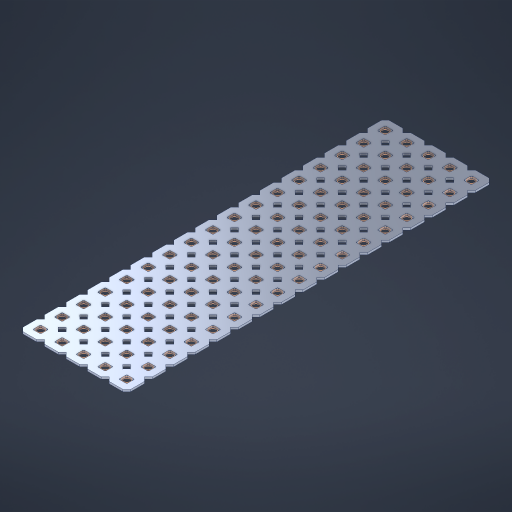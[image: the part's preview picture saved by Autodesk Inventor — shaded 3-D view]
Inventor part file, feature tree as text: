
AUTODESK INVENTOR PART (.ipt)
format: ipt  version: 2023 (Build 270158000, 158)  size: 1,245,696 bytes
history: native  units: in
note: dims shown in document units (in); Inventor stores cm internally (conversion verified against a paired STEP export)
features: other x86, extrude x84, sketch x2, pattern_linear x1
ambient origin geometry x8: Origin, YZ Plane, XZ Plane, XY Plane, X Axis, Y Axis, Z Axis, Center Point
bodies: Solid1 (feature_tree), Body (feature_tree)
feature tree (173):
  pattern_linear  "Rectangular Pattern1"  Spacing1=0.09in  [1 undecoded]
  sketch  "Sketch1"  dims[d1=0.5in]
  sketch  "Sketch2"  dims[d2=0.182in d3=0.09in d4=0.09in d5=0.09in d6=0.09in d7=0.09in d8=0.09in d9=0.09in d10=0.09in d11=0.02in d13=0.0in d14=0.172in d15=0.0625in d16=0.0in d19=0.5in d22=0.5in]
  other  "Srf1"
  other  "Srf126"
  other  "Srf127"
  other  "Srf128"
  other  "Srf129"
  other  "Srf130"
  other  "Srf131"
  other  "Srf250"
  other  "Srf251"
  other  "Srf252"
  other  "Srf253"
  other  "Srf254"
  other  "Srf255"
  other  "Srf256"
  other  "Srf257"
  other  "Srf258"
  other  "Srf259"
  other  "Srf268"
  other  "Srf269"
  other  "Srf270"
  other  "Srf271"
  other  "Srf272"
  other  "Srf273"
  other  "Srf274"
  other  "Srf275"
  other  "Srf276"
  other  "Srf277"
  other  "Srf278"
  other  "Srf279"
  other  "Srf280"
  other  "Srf281"
  other  "Srf282"
  other  "Srf283"
  other  "Srf284"
  other  "Srf293"
  other  "Srf294"
  other  "Srf295"
  other  "Srf296"
  other  "Srf297"
  other  "Srf298"
  other  "Srf299"
  other  "Srf300"
  other  "Srf301"
  other  "Srf302"
  other  "Srf303"
  other  "Srf304"
  other  "Srf305"
  other  "Srf306"
  other  "Srf307"
  other  "Srf308"
  other  "Srf309"
  other  "Srf318"
  other  "Srf319"
  other  "Srf320"
  other  "Srf321"
  other  "Srf322"
  other  "Srf323"
  other  "Srf324"
  other  "Srf325"
  other  "Srf326"
  other  "Srf327"
  other  "Srf328"
  other  "Srf329"
  other  "Srf330"
  other  "Srf331"
  other  "Srf332"
  other  "Srf333"
  other  "Srf334"
  other  "Srf343"
  other  "Srf344"
  other  "Srf345"
  other  "Srf346"
  other  "Srf347"
  other  "Srf348"
  other  "Srf349"
  other  "Srf350"
  other  "Srf351"
  other  "Srf352"
  other  "Srf353"
  other  "Srf354"
  other  "Srf355"
  other  "Srf356"
  other  "Srf357"
  other  "Srf358"
  other  "Srf359"
  other  "Circle"
  extrude  "ExtrusionSrf126"  Depth=0.09in
  extrude  "ExtrusionSrf127"  Depth=0.09in
  extrude  "ExtrusionSrf128"  Depth=0.09in
  extrude  "ExtrusionSrf129"  Depth=0.09in
  extrude  "ExtrusionSrf130"  Depth=0.09in
  extrude  "ExtrusionSrf131"  Depth=0.09in
  extrude  "ExtrusionSrf250"  Depth=0.09in
  extrude  "ExtrusionSrf251"  Depth=0.02in
  extrude  "ExtrusionSrf252"  TaperAngle=0.0deg  [1 undecoded]
  extrude  "ExtrusionSrf253"  Depth=0.5in
  extrude  "ExtrusionSrf254"  Depth=0.5in TaperAngle=0.0deg
  extrude  "ExtrusionSrf255"  Depth=0.5in
  extrude  "ExtrusionSrf256"  Depth=0.5in
  extrude  "ExtrusionSrf257"  [1 undecoded]
  extrude  "ExtrusionSrf258"  [1 undecoded]
  extrude  "ExtrusionSrf259"  [1 undecoded]
  extrude  "ExtrusionSrf268"  [1 undecoded]
  extrude  "ExtrusionSrf269"  [1 undecoded]
  extrude  "ExtrusionSrf270"  [1 undecoded]
  extrude  "ExtrusionSrf271"  [1 undecoded]
  extrude  "ExtrusionSrf272"  [1 undecoded]
  extrude  "ExtrusionSrf273"  [1 undecoded]
  extrude  "ExtrusionSrf274"  [1 undecoded]
  extrude  "ExtrusionSrf275"  [1 undecoded]
  extrude  "ExtrusionSrf276"  [1 undecoded]
  extrude  "ExtrusionSrf277"  [1 undecoded]
  extrude  "ExtrusionSrf278"  [1 undecoded]
  extrude  "ExtrusionSrf279"  [1 undecoded]
  extrude  "ExtrusionSrf280"  [1 undecoded]
  extrude  "ExtrusionSrf281"  [1 undecoded]
  extrude  "ExtrusionSrf282"  [1 undecoded]
  extrude  "ExtrusionSrf283"  [1 undecoded]
  extrude  "ExtrusionSrf284"  [1 undecoded]
  extrude  "ExtrusionSrf293"  [1 undecoded]
  extrude  "ExtrusionSrf294"  [1 undecoded]
  extrude  "ExtrusionSrf295"  [1 undecoded]
  extrude  "ExtrusionSrf296"  [1 undecoded]
  extrude  "ExtrusionSrf297"  [1 undecoded]
  extrude  "ExtrusionSrf298"  [1 undecoded]
  extrude  "ExtrusionSrf299"  [1 undecoded]
  extrude  "ExtrusionSrf300"  [1 undecoded]
  extrude  "ExtrusionSrf301"  [1 undecoded]
  extrude  "ExtrusionSrf302"  [1 undecoded]
  extrude  "ExtrusionSrf303"  [1 undecoded]
  extrude  "ExtrusionSrf304"  [1 undecoded]
  extrude  "ExtrusionSrf305"  [1 undecoded]
  extrude  "ExtrusionSrf306"  [1 undecoded]
  extrude  "ExtrusionSrf307"  [1 undecoded]
  extrude  "ExtrusionSrf308"  [1 undecoded]
  extrude  "ExtrusionSrf309"  [1 undecoded]
  extrude  "ExtrusionSrf318"  [1 undecoded]
  extrude  "ExtrusionSrf319"  [1 undecoded]
  extrude  "ExtrusionSrf320"  [1 undecoded]
  extrude  "ExtrusionSrf321"  [1 undecoded]
  extrude  "ExtrusionSrf322"  [1 undecoded]
  extrude  "ExtrusionSrf323"  [1 undecoded]
  extrude  "ExtrusionSrf324"  [1 undecoded]
  extrude  "ExtrusionSrf325"  [1 undecoded]
  extrude  "ExtrusionSrf326"  [1 undecoded]
  extrude  "ExtrusionSrf327"  [1 undecoded]
  extrude  "ExtrusionSrf328"  [1 undecoded]
  extrude  "ExtrusionSrf329"  [1 undecoded]
  extrude  "ExtrusionSrf330"  [1 undecoded]
  extrude  "ExtrusionSrf331"  [1 undecoded]
  extrude  "ExtrusionSrf332"  [1 undecoded]
  extrude  "ExtrusionSrf333"  [1 undecoded]
  extrude  "ExtrusionSrf334"  [1 undecoded]
  extrude  "ExtrusionSrf343"  [1 undecoded]
  extrude  "ExtrusionSrf344"  [1 undecoded]
  extrude  "ExtrusionSrf345"  [1 undecoded]
  extrude  "ExtrusionSrf346"  [1 undecoded]
  extrude  "ExtrusionSrf347"  [1 undecoded]
  extrude  "ExtrusionSrf348"  [1 undecoded]
  extrude  "ExtrusionSrf349"  [1 undecoded]
  extrude  "ExtrusionSrf350"  [1 undecoded]
  extrude  "ExtrusionSrf351"  [1 undecoded]
  extrude  "ExtrusionSrf352"  [1 undecoded]
  extrude  "ExtrusionSrf353"  [1 undecoded]
  extrude  "ExtrusionSrf354"  [1 undecoded]
  extrude  "ExtrusionSrf355"  [1 undecoded]
  extrude  "ExtrusionSrf356"  [1 undecoded]
  extrude  "ExtrusionSrf357"  [1 undecoded]
  extrude  "ExtrusionSrf358"  [1 undecoded]
  extrude  "ExtrusionSrf359"  [1 undecoded]
note: 73 required parameter values undecoded (feature->parameter linkage not recoverable at this tier; creation-order binding heuristic only, values carry confidence <= 0.55)
